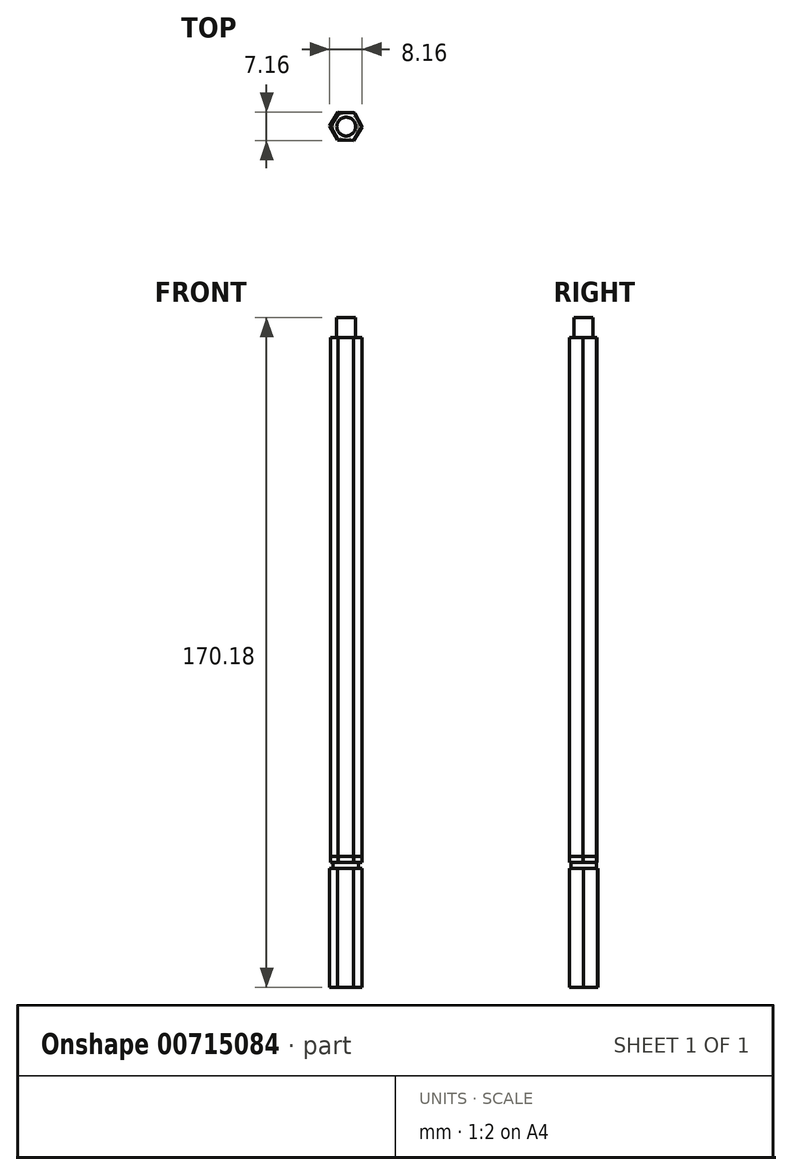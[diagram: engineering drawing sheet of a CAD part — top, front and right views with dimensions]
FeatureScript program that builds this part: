
annotation { "Feature Type Name" : "Feature", "Feature Type Description" : "" }
export const myFeature = defineFeature(function(context is Context, id is Id, definition is map)
    precondition{}
    {
        {
            var Q0;
            Q0=qCreatedBy(makeId("Top.planeOp"),FACE);
            var sketch = newSketch(context, id + "F0", { "sketchPlane" : qUnion([Q0])});
            skCircle(sketch, "E0.cCircle", {"center": v(-43.44, 40.39) * mm, "radius": 3.44 * mm, "construction": true});
            skLineSegment(sketch, "E0.0", {"start": v(-39.48, 40.25) * mm, "end": v(-41.58, 36.88) * mm});
            skLineSegment(sketch, "E0.1", {"start": v(-41.58, 36.88) * mm, "end": v(-45.55, 37.02) * mm});
            skLineSegment(sketch, "E0.2", {"start": v(-45.55, 37.02) * mm, "end": v(-47.41, 40.53) * mm});
            skLineSegment(sketch, "E0.3", {"start": v(-47.41, 40.53) * mm, "end": v(-45.3, 43.9) * mm});
            skLineSegment(sketch, "E0.4", {"start": v(-45.3, 43.9) * mm, "end": v(-41.34, 43.75) * mm});
            skLineSegment(sketch, "E0.5", {"start": v(-41.34, 43.75) * mm, "end": v(-39.48, 40.25) * mm});
            skPoint(sketch, "E0.0.midPoint", {"position": v(-40.53, 38.57) * mm});
            skSolve(sketch);
        }
        {
            var Q0;
            Q0=makeQuery(id+"F0.imprint","IMPRINT",FACE,{"disambiguationData":[TD([[makeQuery(id+"F0.imprint","IMPRINT",EDGE,{"derivedFrom":sQuery(id+"F0.wireOp",EDGE,"E0.0")}),-1.0]])]});
            extrude(context, id + "F1", {"entities" : qUnion([Q0]), "oppositeDirection" : true, "depth" : 133.35 * mm, "offsetDistance" : 25.4 * mm});
        }
        {
            var Q0;
            Q0=makeQuery(id+"F1.opExtrude","CAP_FACE",FACE,{"disambiguationData":[OSD([sQuery(id+"F0.wireOp",EDGE,"E0.0"),sQuery(id+"F0.wireOp",EDGE,"E0.1"),sQuery(id+"F0.wireOp",EDGE,"E0.2"),sQuery(id+"F0.wireOp",EDGE,"E0.3"),sQuery(id+"F0.wireOp",EDGE,"E0.4"),sQuery(id+"F0.wireOp",EDGE,"E0.5")])],"isStart":true});
            var sketch = newSketch(context, id + "F2", { "sketchPlane" : qUnion([Q0])});
            skCircle(sketch, "E1", {"center": v(-43.47, 40.39) * mm, "radius": 2.38 * mm});
            skSolve(sketch);
        }
        {
            var Q0;
            Q0=makeQuery(id+"F2.imprint","IMPRINT",FACE,{"disambiguationData":[TD([[makeQuery(id+"F2.imprint","IMPRINT",EDGE,{"derivedFrom":sQuery(id+"F2.wireOp",EDGE,"E1")}),1.0]])]});
            extrude(context, id + "F3", {"entities" : qUnion([Q0]), "operationType" : NewBodyOperationType.ADD, "depth" : 5.08 * mm, "offsetDistance" : 25.4 * mm});
        }
        {
            var Q0;
            Q0=makeQuery(id+"F1.opExtrude","CAP_FACE",FACE,{"disambiguationData":[OSD([sQuery(id+"F0.wireOp",EDGE,"E0.0"),sQuery(id+"F0.wireOp",EDGE,"E0.1"),sQuery(id+"F0.wireOp",EDGE,"E0.2"),sQuery(id+"F0.wireOp",EDGE,"E0.3"),sQuery(id+"F0.wireOp",EDGE,"E0.4"),sQuery(id+"F0.wireOp",EDGE,"E0.5")])],"isStart":false});
            extrude(context, id + "F4", {"entities" : qUnion([Q0]), "oppositeDirection" : true, "depth" : 1.52 * mm, "offsetDistance" : 25.4 * mm});
        }
        {
            var Q0;
            Q0=makeQuery(id+"F1.opExtrude","CAP_FACE",FACE,{"disambiguationData":[OSD([sQuery(id+"F0.wireOp",EDGE,"E0.0"),sQuery(id+"F0.wireOp",EDGE,"E0.1"),sQuery(id+"F0.wireOp",EDGE,"E0.2"),sQuery(id+"F0.wireOp",EDGE,"E0.3"),sQuery(id+"F0.wireOp",EDGE,"E0.4"),sQuery(id+"F0.wireOp",EDGE,"E0.5")])],"isStart":false});
            var sketch = newSketch(context, id + "F5", { "sketchPlane" : qUnion([Q0])});
            skCircle(sketch, "E2", {"center": v(-43.57, -40.45) * mm, "radius": 3.27 * mm});
            skPoint(sketch, "E2.centerSnap0", {"position": v(-43.57, -36.95) * mm});
            skSolve(sketch);
        }
        {
            var Q0;
            Q0 = qSketchRegion(id + "F5", true);
            extrude(context, id + "F6", {"entities" : qUnion([Q0]), "depth" : 1.52 * mm, "offsetDistance" : 25.4 * mm});
        }
        {
            var Q0;
            Q0=makeQuery(id+"F6.opExtrude","CAP_FACE",FACE,{"disambiguationData":[OSD([sQuery(id+"F5.wireOp",EDGE,"E2")])],"isStart":false});
            var sketch = newSketch(context, id + "F7", { "sketchPlane" : qUnion([Q0])});
            skCircle(sketch, "E3.cCircle", {"center": v(-43.57, -40.45) * mm, "radius": 3.53 * mm, "construction": true});
            skLineSegment(sketch, "E3.0", {"start": v(-41.61, -36.87) * mm, "end": v(-39.49, -40.36) * mm});
            skLineSegment(sketch, "E3.1", {"start": v(-39.49, -40.36) * mm, "end": v(-41.44, -43.93) * mm});
            skLineSegment(sketch, "E3.2", {"start": v(-41.44, -43.93) * mm, "end": v(-45.52, -44.03) * mm});
            skLineSegment(sketch, "E3.3", {"start": v(-45.52, -44.03) * mm, "end": v(-47.64, -40.55) * mm});
            skLineSegment(sketch, "E3.4", {"start": v(-47.64, -40.55) * mm, "end": v(-45.69, -36.97) * mm});
            skLineSegment(sketch, "E3.5", {"start": v(-45.69, -36.97) * mm, "end": v(-41.61, -36.87) * mm});
            skPoint(sketch, "E3.0.midPoint", {"position": v(-40.55, -38.61) * mm});
            skSolve(sketch);
        }
        {
            var Q0;
            Q0 = qSketchRegion(id + "F7", true);
            extrude(context, id + "F8", {"entities" : qUnion([Q0]), "operationType" : NewBodyOperationType.ADD, "depth" : 30.23 * mm, "offsetDistance" : 25.4 * mm});
        }
    });
